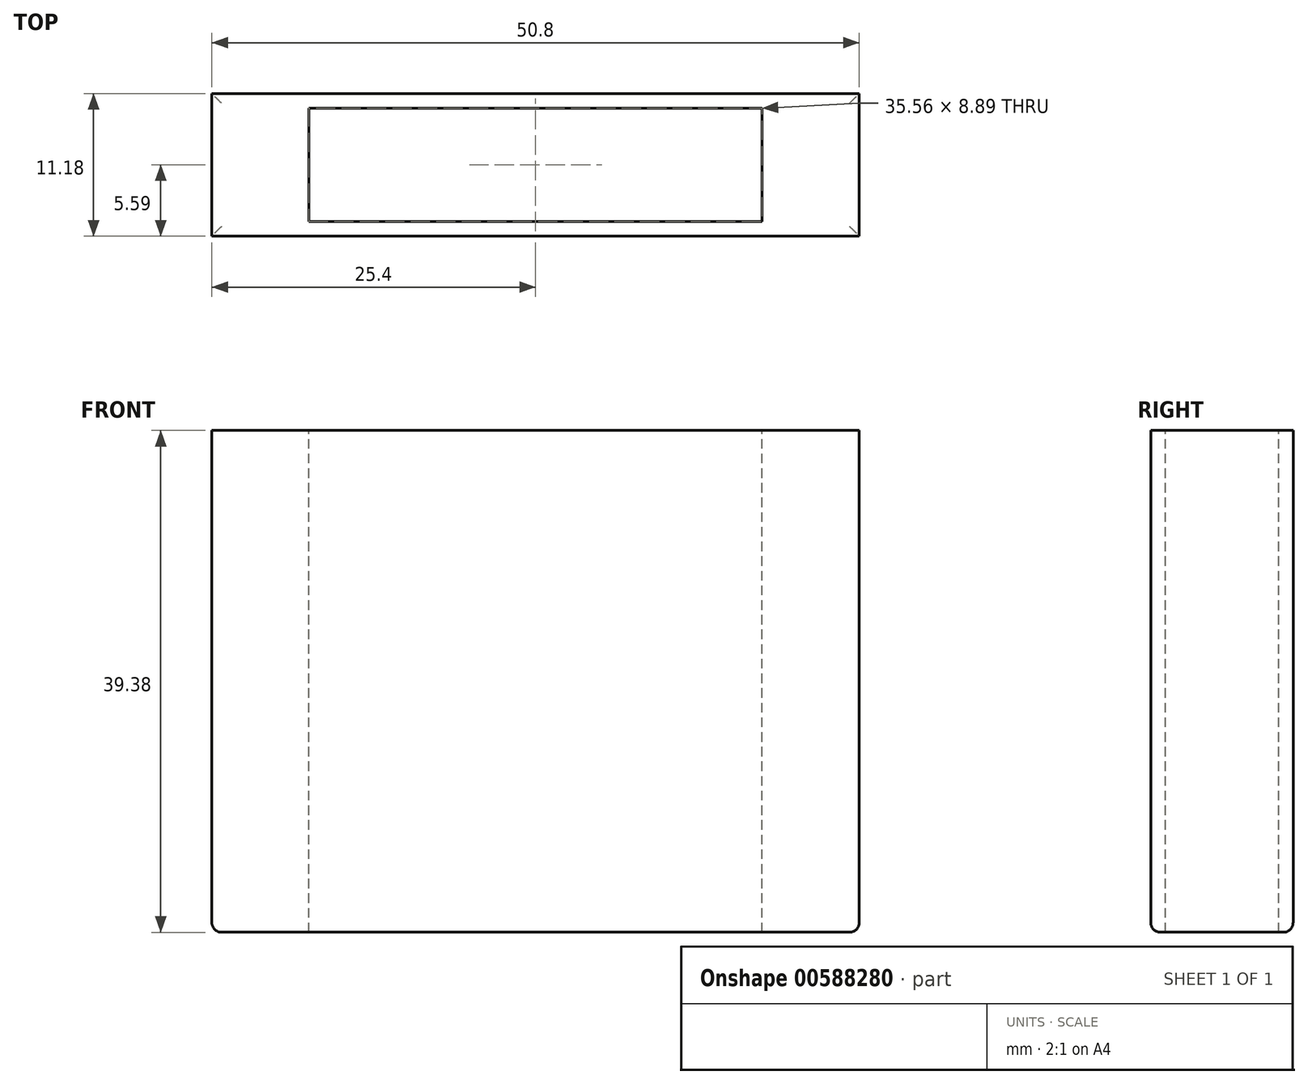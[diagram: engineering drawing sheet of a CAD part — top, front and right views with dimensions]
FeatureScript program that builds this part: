
annotation { "Feature Type Name" : "Feature", "Feature Type Description" : "" }
export const myFeature = defineFeature(function(context is Context, id is Id, definition is map)
    precondition{}
    {
        {
            var Q0;
            Q0=qCreatedBy(makeId("Front.planeOp"),FACE);
            var sketch = newSketch(context, id + "F0", { "sketchPlane" : qUnion([Q0])});
            skLineSegment(sketch, "E0.bottom", {"start": v(-25.4, 19.69) * mm, "end": v(25.4, 19.69) * mm});
            skLineSegment(sketch, "E0.top", {"start": v(-25.4, -19.68) * mm, "end": v(25.4, -19.68) * mm});
            skLineSegment(sketch, "E0.left", {"start": v(-25.4, 19.69) * mm, "end": v(-25.4, -19.68) * mm});
            skLineSegment(sketch, "E0.right", {"start": v(25.4, 19.69) * mm, "end": v(25.4, -19.68) * mm});
            skPoint(sketch, "E0.middle", {"position": v(0, 0) * mm});
            skSolve(sketch);
        }
        {
            var Q0;
            Q0=makeQuery(id+"F0.imprint","IMPRINT",FACE,{"disambiguationData":[TD([[makeQuery(id+"F0.imprint","IMPRINT",EDGE,{"derivedFrom":sQuery(id+"F0.wireOp",EDGE,"E0.bottom")}),-1.0]])]});
            extrude(context, id + "F1", {"entities" : qUnion([Q0]), "endBound" : BoundingType.SYMMETRIC, "depth" : 11.18 * mm, "offsetDistance" : 25.4 * mm});
        }
        {
            var Q0;
            Q0=makeQuery(id+"F1.opExtrude","SWEPT_FACE",FACE,{"disambiguationData":[OSD([sQuery(id+"F0.wireOp",EDGE,"E0.bottom")])]});
            var sketch = newSketch(context, id + "F2", { "sketchPlane" : qUnion([Q0])});
            skLineSegment(sketch, "E1.bottom", {"start": v(17.78, 4.45) * mm, "end": v(-17.78, 4.45) * mm});
            skLineSegment(sketch, "E1.top", {"start": v(17.78, -4.45) * mm, "end": v(-17.78, -4.45) * mm});
            skLineSegment(sketch, "E1.left", {"start": v(17.78, 4.45) * mm, "end": v(17.78, -4.45) * mm});
            skLineSegment(sketch, "E1.right", {"start": v(-17.78, 4.45) * mm, "end": v(-17.78, -4.45) * mm});
            skPoint(sketch, "E1.middle", {"position": v(0, 0) * mm});
            skSolve(sketch);
        }
        {
            var Q0;
            Q0=makeQuery(id+"F2.imprint","IMPRINT",FACE,{"disambiguationData":[TD([[makeQuery(id+"F2.imprint","IMPRINT",EDGE,{"derivedFrom":sQuery(id+"F2.wireOp",EDGE,"E1.bottom")}),1.0]])]});
            extrude(context, id + "F3", {"entities" : qUnion([Q0]), "operationType" : NewBodyOperationType.REMOVE, "oppositeDirection" : true, "depth" : 39.37 * mm, "offsetDistance" : 25.4 * mm});
        }
        {
            var Q0;
            Q0=makeQuery(id+"F1.opExtrude","SWEPT_EDGE",EDGE,{"disambiguationData":[OSD([sQuery(id+"F0.wireOp",EDGE,"E0.top"),sQuery(id+"F0.wireOp",EDGE,"E0.right")])]});
            var Q1;
            Q1=makeQuery(id+"F1.opExtrude","CAP_EDGE",EDGE,{"disambiguationData":[OSD([sQuery(id+"F0.wireOp",EDGE,"E0.top")])],"isStart":false});
            var Q2;
            Q2=makeQuery(id+"F1.opExtrude","CAP_EDGE",EDGE,{"disambiguationData":[OSD([sQuery(id+"F0.wireOp",EDGE,"E0.top")])],"isStart":true});
            var Q3;
            Q3=makeQuery(id+"F1.opExtrude","SWEPT_EDGE",EDGE,{"disambiguationData":[OSD([sQuery(id+"F0.wireOp",EDGE,"E0.top"),sQuery(id+"F0.wireOp",EDGE,"E0.left")])]});
            fillet(context, id + "F4", {"entities" : qUnion([Q0, Q1, Q2, Q3]), "radius" : 0.76 * mm, "tangentPropagation" : true, "allowEdgeOverflow" : false});
        }
    });
